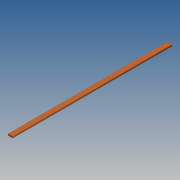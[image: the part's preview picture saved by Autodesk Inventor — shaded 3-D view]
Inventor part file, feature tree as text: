
AUTODESK INVENTOR PART (.ipt)
format: ipt  version: 2013 SP2 (Build 170200200, 200)  size: 81,920 bytes
history: native  units: in
note: dims shown in document units (in); Inventor stores cm internally (conversion verified against a paired STEP export)
features: sketch x3, hole x2, extrude x1
ambient origin geometry x8: Origin, YZ Plane, XZ Plane, XY Plane, X Axis, Y Axis, Z Axis, Center Point
bodies: Solid1 (feature_tree)
feature tree (6):
  extrude  "Extrusion1"  Depth=0.5in
  hole  "Hole1"  [1 undecoded]
  hole  "Hole2"  [1 undecoded]
  sketch  "Sketch1"  dims[d0=1.5in d1=0.5in]
  sketch  "Sketch2"  dims[d2=50.0in d3=0.0in d4=0.5in]
  sketch  "Sketch3"  dims[d5=0.125in d6=0.75in d7=0.375in d8=0.25in d9=0.5635in d10=1.0in d11=0.8108in d12=0.5in d13=0.125in d14=0.75in d15=0.375in d16=0.25in d17=0.5635in d18=1.0in d19=0.8108in]
note: 2 required parameter values undecoded (feature->parameter linkage not recoverable at this tier; creation-order binding heuristic only, values carry confidence <= 0.55)
